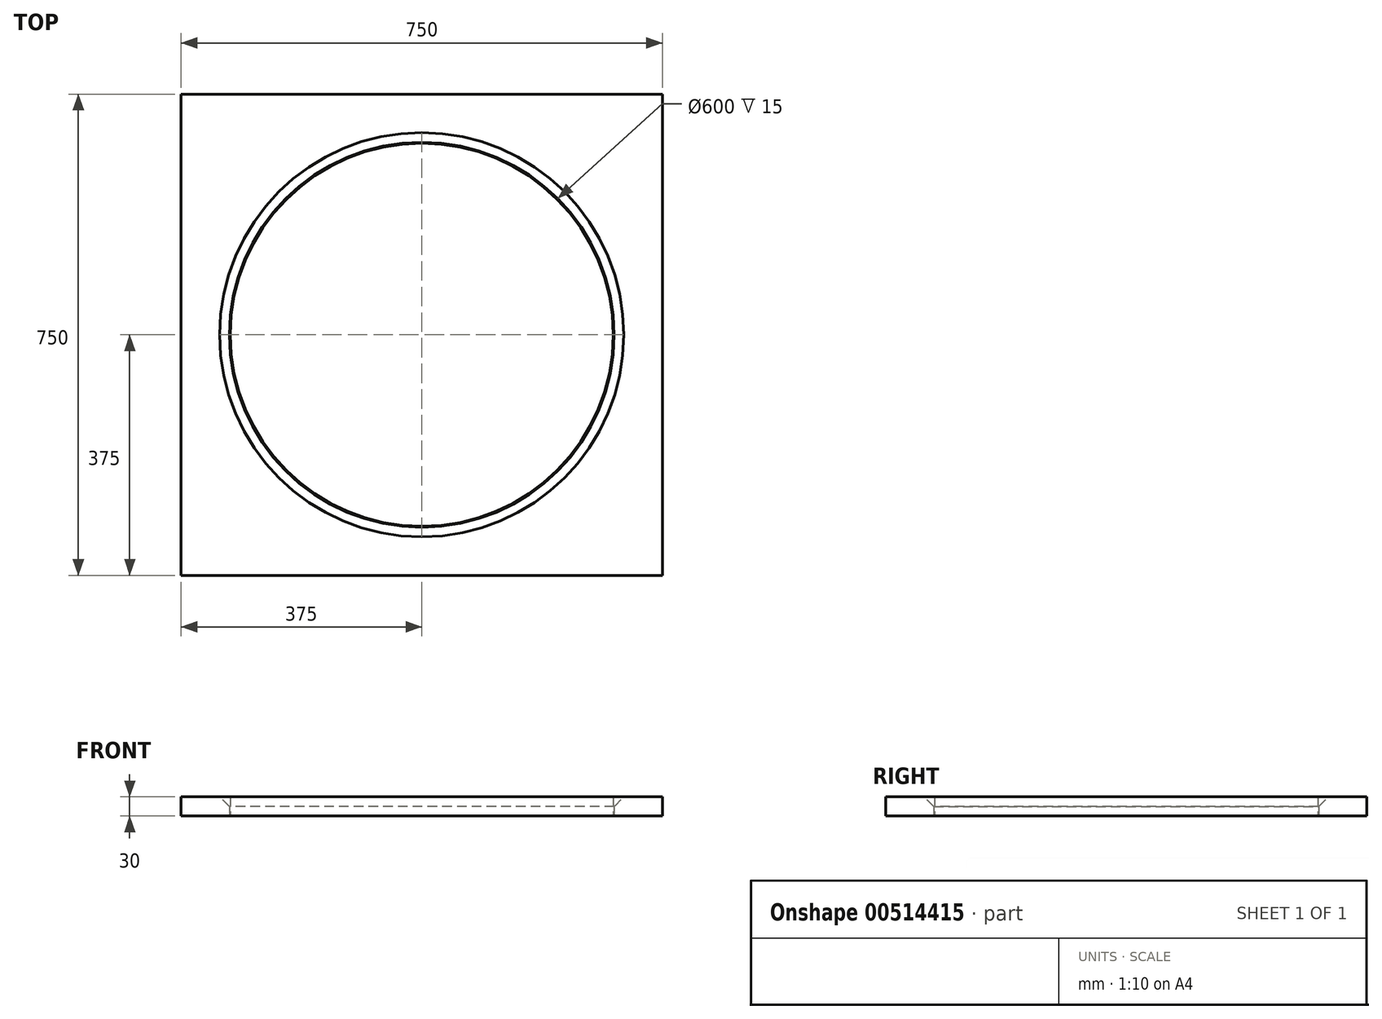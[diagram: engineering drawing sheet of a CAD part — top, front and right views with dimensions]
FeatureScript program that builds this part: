
annotation { "Feature Type Name" : "Feature", "Feature Type Description" : "" }
export const myFeature = defineFeature(function(context is Context, id is Id, definition is map)
    precondition{}
    {
        {
            var Q0;
            Q0=qCreatedBy(makeId("Top.planeOp"),FACE);
            var sketch = newSketch(context, id + "F0", { "sketchPlane" : qUnion([Q0])});
            skCircle(sketch, "E0", {"center": v(0, 0) * mm, "radius": 300 * mm});
            skLineSegment(sketch, "E1.bottom", {"start": v(-375, -375) * mm, "end": v(375, -375) * mm});
            skLineSegment(sketch, "E1.top", {"start": v(-375, 375) * mm, "end": v(375, 375) * mm});
            skLineSegment(sketch, "E1.left", {"start": v(-375, -375) * mm, "end": v(-375, 375) * mm});
            skLineSegment(sketch, "E1.right", {"start": v(375, -375) * mm, "end": v(375, 375) * mm});
            skCircle(sketch, "E2", {"center": v(0, 0) * mm, "radius": 298.5 * mm});
            skSolve(sketch);
        }
        {
            var Q0;
            Q0=makeQuery(id+"F0.imprint","IMPRINT",FACE,{"disambiguationData":[TD([[makeQuery(id+"F0.imprint","IMPRINT",EDGE,{"derivedFrom":sQuery(id+"F0.wireOp",EDGE,"E0")}),-1.0]])]});
            var Q1;
            Q1=makeQuery(id+"F0.imprint","IMPRINT",FACE,{"disambiguationData":[TD([[makeQuery(id+"F0.imprint","IMPRINT",EDGE,{"derivedFrom":sQuery(id+"F0.wireOp",EDGE,"E2")}),1.0]])]});
            extrude(context, id + "F1", {"entities" : qUnion([Q0, Q1]), "depth" : 30 * mm, "offsetDistance" : 25 * mm});
        }
        {
            var Q0;
            Q0=makeQuery(id+"F1.opExtrude","CAP_EDGE",EDGE,{"disambiguationData":[OSD([sQuery(id+"F0.wireOp",EDGE,"E0")])],"isStart":false});
            chamfer(context, id + "F2", {"entities" : qUnion([Q0]), "width" : 15 * mm, "tangentPropagation" : true});
        }
    });
